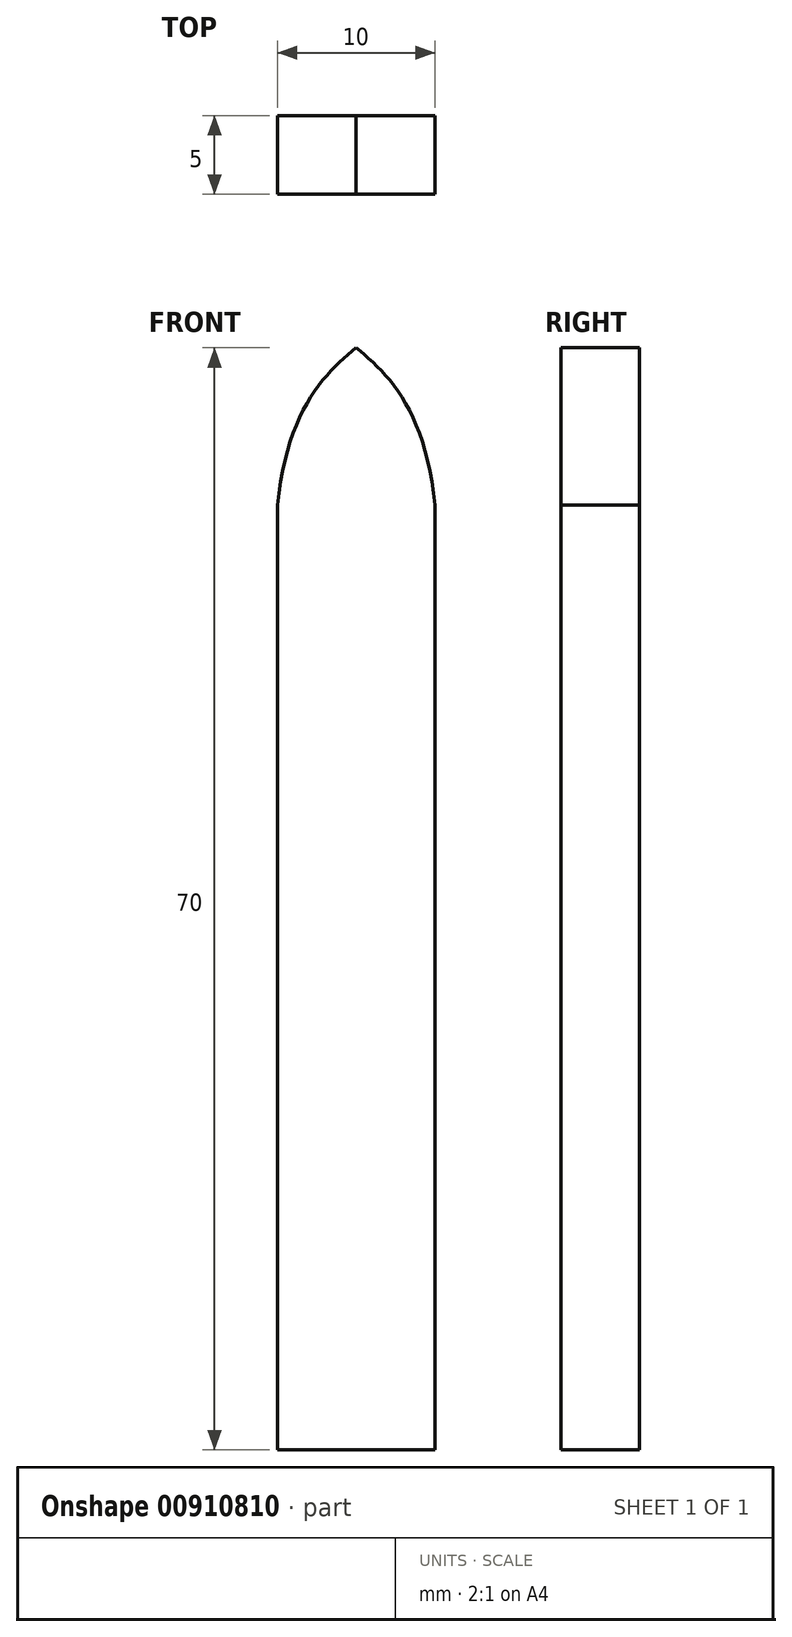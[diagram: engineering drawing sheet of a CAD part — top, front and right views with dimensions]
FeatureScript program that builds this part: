
annotation { "Feature Type Name" : "Feature", "Feature Type Description" : "" }
export const myFeature = defineFeature(function(context is Context, id is Id, definition is map)
    precondition{}
    {
        {
            var Q0;
            Q0=qCreatedBy(makeId("Front.planeOp"),FACE);
            var sketch = newSketch(context, id + "F0", { "sketchPlane" : qUnion([Q0])});
            skLineSegment(sketch, "E0.bottom", {"start": v(5, 35) * mm, "end": v(-5, 35) * mm});
            skLineSegment(sketch, "E0.top", {"start": v(5, -35) * mm, "end": v(-5, -35) * mm});
            skLineSegment(sketch, "E0.left", {"start": v(5, 35) * mm, "end": v(5, -35) * mm});
            skLineSegment(sketch, "E0.right", {"start": v(-5, 35) * mm, "end": v(-5, -35) * mm});
            skPoint(sketch, "E0.middle", {"position": v(0, 0) * mm});
            skFitSpline(sketch, "E1", {"points": [v(-5, 25) * mm, v(0, 35) * mm], "startDerivative": vector(1.84, 18.18) * mm, "endDerivative": vector(5.97, 4.79) * mm});
            skFitSpline(sketch, "E2.MirrorCS", {"points": [v(5, 25) * mm, v(0, 35) * mm], "startDerivative": vector(-1.84, 18.18) * mm, "endDerivative": vector(-5.97, 4.79) * mm});
            skSolve(sketch);
        }
        {
            var Q0;
            {var subQ1=sQuery(id+"F0.wireOp",EDGE,"E0.top");Q0=makeQuery(id+"F0.imprint","IMPRINT",FACE,{"disambiguationData":[TD([[makeQuery(id+"F0.imprint","IMPRINT",EDGE,{"derivedFrom":subQ1}),-1.0]])]});}
            var Q1;
            {var subQ3=sQuery(id+"F0.wireOp",EDGE,"E2.MirrorCS");Q1=makeQuery(id+"F0.imprint","IMPRINT",FACE,{"disambiguationData":[TD([[makeQuery(id+"F0.imprint","IMPRINT",EDGE,{"derivedFrom":subQ3}),-1.0]])]});}
            var Q2;
            {var subQ3=sQuery(id+"F0.wireOp",EDGE,"E1");Q2=makeQuery(id+"F0.imprint","IMPRINT",FACE,{"disambiguationData":[TD([[makeQuery(id+"F0.imprint","IMPRINT",EDGE,{"derivedFrom":subQ3}),1.0]])]});}
            extrude(context, id + "F1", {"entities" : qUnion([Q0, Q1, Q2]), "depth" : 5 * mm, "offsetDistance" : 25 * mm});
        }
        {
            var Q0;
            {var subQ3=sQuery(id+"F0.wireOp",EDGE,"E1");Q0=makeQuery(id+"F0.imprint","IMPRINT",FACE,{"disambiguationData":[TD([[makeQuery(id+"F0.imprint","IMPRINT",EDGE,{"derivedFrom":subQ3}),1.0]])]});}
            extrude(context, id + "F2", {"entities" : qUnion([Q0]), "operationType" : NewBodyOperationType.REMOVE, "depth" : 25 * mm, "offsetDistance" : 25 * mm, "hasSecondDirection" : true, "secondDirectionBound" : SecondDirectionBoundingType.THROUGH_ALL, "secondDirectionOppositeDirection" : true, "secondDirectionDepth" : 25 * mm});
        }
        {
            var Q0;
            {var subQ3=sQuery(id+"F0.wireOp",EDGE,"E2.MirrorCS");Q0=makeQuery(id+"F0.imprint","IMPRINT",FACE,{"disambiguationData":[TD([[makeQuery(id+"F0.imprint","IMPRINT",EDGE,{"derivedFrom":subQ3}),-1.0]])]});}
            extrude(context, id + "F3", {"entities" : qUnion([Q0]), "operationType" : NewBodyOperationType.REMOVE, "endBound" : BoundingType.THROUGH_ALL, "oppositeDirection" : true, "depth" : 25 * mm, "offsetDistance" : 25 * mm, "hasSecondDirection" : true, "secondDirectionBound" : SecondDirectionBoundingType.THROUGH_ALL, "secondDirectionOppositeDirection" : false, "secondDirectionDepth" : 25 * mm});
        }
    });
